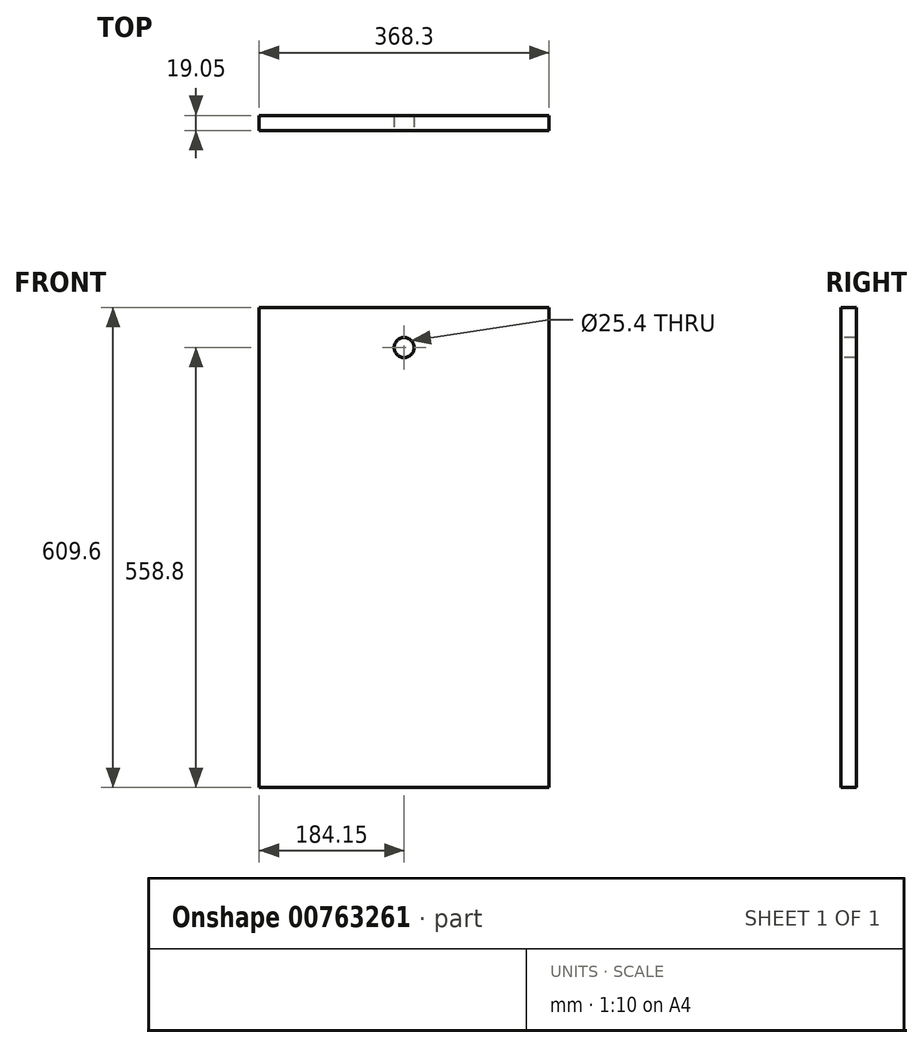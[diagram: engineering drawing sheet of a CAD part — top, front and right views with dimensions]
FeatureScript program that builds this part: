
annotation { "Feature Type Name" : "Feature", "Feature Type Description" : "" }
export const myFeature = defineFeature(function(context is Context, id is Id, definition is map)
    precondition{}
    {
        {
            var Q0;
            Q0=qCreatedBy(makeId("Front.planeOp"),FACE);
            var sketch = newSketch(context, id + "F0", { "sketchPlane" : qUnion([Q0])});
            skLineSegment(sketch, "E0.bottom", {"start": v(184.15, 304.8) * mm, "end": v(-184.15, 304.8) * mm});
            skLineSegment(sketch, "E0.top", {"start": v(184.15, -304.8) * mm, "end": v(-184.15, -304.8) * mm});
            skLineSegment(sketch, "E0.left", {"start": v(184.15, 304.8) * mm, "end": v(184.15, -304.8) * mm});
            skLineSegment(sketch, "E0.right", {"start": v(-184.15, 304.8) * mm, "end": v(-184.15, -304.8) * mm});
            skPoint(sketch, "E0.middle", {"position": v(0, 0) * mm});
            skSolve(sketch);
        }
        {
            var Q0;
            Q0=qSketchRegion(id+"F0",true);
            extrude(context, id + "F1", {"entities" : qUnion([Q0]), "depth" : 19.05 * mm, "offsetDistance" : 25.4 * mm});
        }
        {
            var Q0;
            Q0=makeQuery(id+"F1.opExtrude","CAP_FACE",FACE,{"disambiguationData":[OSD([sQuery(id+"F0.wireOp",EDGE,"E0.bottom"),sQuery(id+"F0.wireOp",EDGE,"E0.top"),sQuery(id+"F0.wireOp",EDGE,"E0.left"),sQuery(id+"F0.wireOp",EDGE,"E0.right")])],"isStart":false});
            var sketch = newSketch(context, id + "F2", { "sketchPlane" : qUnion([Q0])});
            skCircle(sketch, "E1", {"center": v(0, 254) * mm, "radius": 12.7 * mm});
            skSolve(sketch);
        }
        {
            var Q0;
            Q0 = qSketchRegion(id + "F2", true);
            extrude(context, id + "F3", {"entities" : qUnion([Q0]), "operationType" : NewBodyOperationType.REMOVE, "endBound" : BoundingType.THROUGH_ALL, "oppositeDirection" : true, "depth" : 25.4 * mm, "offsetDistance" : 25.4 * mm});
        }
    });
